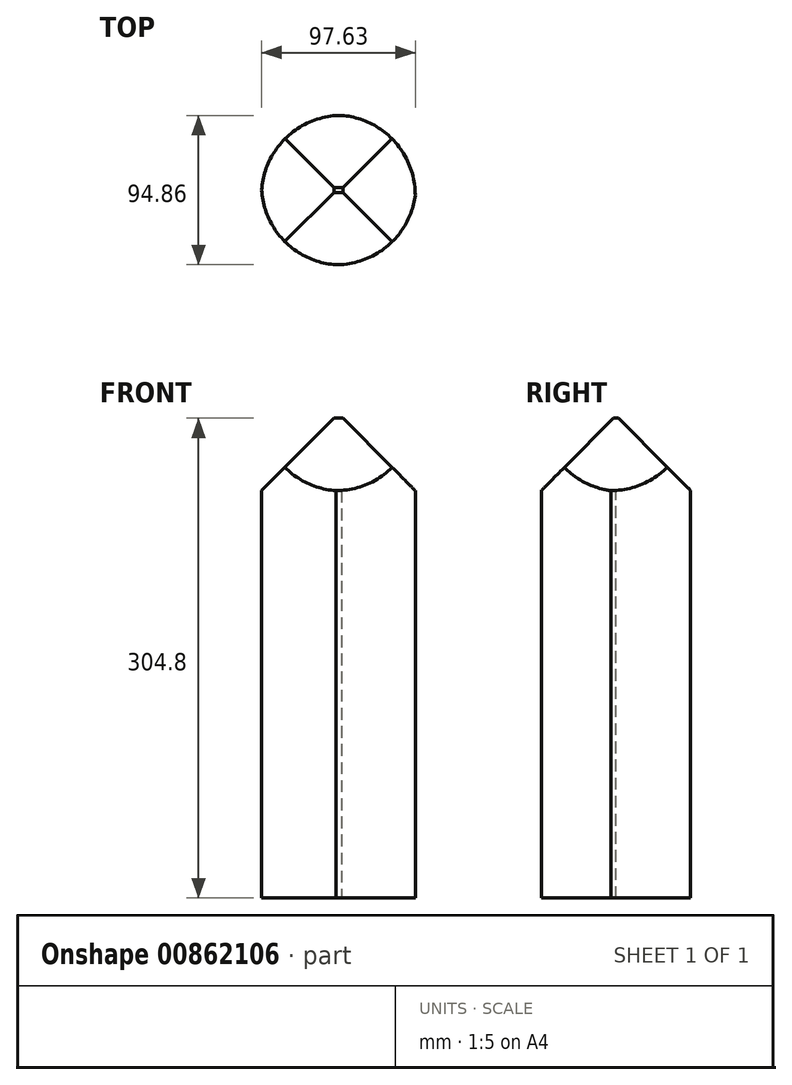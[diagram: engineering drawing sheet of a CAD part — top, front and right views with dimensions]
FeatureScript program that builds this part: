
annotation { "Feature Type Name" : "Feature", "Feature Type Description" : "" }
export const myFeature = defineFeature(function(context is Context, id is Id, definition is map)
    precondition{}
    {
        {
            var Q0;
            Q0=qCreatedBy(makeId("Top.planeOp"),FACE);
            var sketch = newSketch(context, id + "F0", { "sketchPlane" : qUnion([Q0])});
            skLineSegment(sketch, "E0.bottom", {"start": v(-74.27, 76.89) * mm, "end": v(-45.44, 76.89) * mm});
            skLineSegment(sketch, "E0.top", {"start": v(-74.27, 39.29) * mm, "end": v(-45.44, 39.29) * mm});
            skLineSegment(sketch, "E0.left", {"start": v(-74.27, 76.89) * mm, "end": v(-74.27, 39.29) * mm});
            skLineSegment(sketch, "E0.right", {"start": v(-45.44, 76.89) * mm, "end": v(-45.44, 39.29) * mm});
            skLineSegment(sketch, "E1.bottom", {"start": v(-45.44, 39.29) * mm, "end": v(52.3, 39.29) * mm});
            skLineSegment(sketch, "E1.top", {"start": v(-45.44, -55.57) * mm, "end": v(52.3, -55.57) * mm});
            skLineSegment(sketch, "E1.left", {"start": v(-45.44, 39.29) * mm, "end": v(-45.44, -55.57) * mm});
            skLineSegment(sketch, "E1.right", {"start": v(52.3, 39.29) * mm, "end": v(52.3, -55.57) * mm});
            skSolve(sketch);
        }
        {
            var Q0;
            Q0=makeQuery(id+"F0.imprint","IMPRINT",FACE,{"disambiguationData":[TD([[makeQuery(id+"F0.imprint","IMPRINT",EDGE,{"derivedFrom":sQuery(id+"F0.wireOp",EDGE,"E1.bottom")}),-1.0]])]});
            var Q1;
            Q1=makeQuery(id+"F0.imprint","IMPRINT",FACE,{"disambiguationData":[TD([[makeQuery(id+"F0.imprint","IMPRINT",EDGE,{"derivedFrom":sQuery(id+"F0.wireOp",EDGE,"E0.bottom")}),-1.0]])]});
            extrude(context, id + "F1", {"entities" : qUnion([Q0, Q1]), "depth" : 304.8 * mm, "offsetDistance" : 25.4 * mm});
        }
        {
            var Q0;
            Q0=makeQuery(id+"F1.opExtrude","SWEPT_FACE",FACE,{"disambiguationData":[OSD([sQuery(id+"F0.wireOp",EDGE,"E1.right")])]});
            var sketch = newSketch(context, id + "F2", { "sketchPlane" : qUnion([Q0])});
            skLineSegment(sketch, "E2.bottom", {"start": v(-15.23, 174.67) * mm, "end": v(-55.57, 174.67) * mm});
            skLineSegment(sketch, "E2.top", {"start": v(-15.23, 71.74) * mm, "end": v(-55.57, 71.74) * mm});
            skLineSegment(sketch, "E2.left", {"start": v(-15.23, 174.67) * mm, "end": v(-15.23, 71.74) * mm});
            skLineSegment(sketch, "E2.right", {"start": v(-55.57, 174.67) * mm, "end": v(-55.57, 71.74) * mm});
            skSolve(sketch);
        }
        {
            var Q0;
            Q0=makeQuery(id+"F2.imprint","IMPRINT",FACE,{"disambiguationData":[TD([[makeQuery(id+"F2.imprint","IMPRINT",EDGE,{"derivedFrom":sQuery(id+"F2.wireOp",EDGE,"E2.bottom")}),1.0]])]});
            extrude(context, id + "F3", {"entities" : qUnion([Q0]), "operationType" : NewBodyOperationType.ADD, "depth" : -76.2 * mm, "offsetDistance" : 25.4 * mm});
        }
        {
            var Q0;
            Q0=makeQuery(id+"F1.opExtrude","SWEPT_FACE",FACE,{"disambiguationData":[OSD([sQuery(id+"F0.wireOp",EDGE,"E1.top")])]});
            var sketch = newSketch(context, id + "F4", { "sketchPlane" : qUnion([Q0])});
            skCircle(sketch, "E3", {"center": v(0, 202.13) * mm, "radius": 27.07 * mm});
            skSolve(sketch);
        }
        {
            var Q0;
            Q0=sQuery(id+"F4.wireOp",EDGE,"E3");
            extrude(context, id + "F5", {"bodyType" : ToolBodyType.SURFACE, "surfaceEntities" : qUnion([Q0]), "depth" : 304.8 * mm, "offsetDistance" : 25.4 * mm});
        }
        {
            var Q0;
            Q0=makeQuery(id+"F5.opExtrude","SWEPT_BODY",BODY,{"disambiguationData":[OSD([sQuery(id+"F4.wireOp",EDGE,"E3")])]});
            deleteBodies(context, id + "F6", {"entities" : qUnion([Q0])});
        }
        {
            var Q0;
            Q0=makeQuery(id+"F1.opExtrude","SWEPT_BODY",BODY,{"disambiguationData":[OSD([sQuery(id+"F0.wireOp",EDGE,"E0.bottom"),sQuery(id+"F0.wireOp",EDGE,"E0.top"),sQuery(id+"F0.wireOp",EDGE,"E0.left"),sQuery(id+"F0.wireOp",EDGE,"E0.right")])]});
            deleteBodies(context, id + "F7", {"entities" : qUnion([Q0])});
        }
        {
            var Q0;
            Q0=makeQuery(id+"F1.opExtrude","CAP_FACE",FACE,{"disambiguationData":[OSD([sQuery(id+"F0.wireOp",EDGE,"E1.bottom"),sQuery(id+"F0.wireOp",EDGE,"E1.top"),sQuery(id+"F0.wireOp",EDGE,"E1.left"),sQuery(id+"F0.wireOp",EDGE,"E1.right")])],"isStart":false});
            chamfer(context, id + "F8", {"entities" : qUnion([Q0]), "width" : 45.97 * mm, "tangentPropagation" : true});
        }
        {
            var Q0;
            Q0=makeQuery(id+"F1.opExtrude","SWEPT_EDGE",EDGE,{"disambiguationData":[OSD([sQuery(id+"F0.wireOp",EDGE,"E0.top"),sQuery(id+"F0.wireOp",EDGE,"E0.right"),sQuery(id+"F0.wireOp",EDGE,"E1.bottom"),sQuery(id+"F0.wireOp",EDGE,"E1.left")]),OD(1.0)]});
            fillet(context, id + "F9", {"entities" : qUnion([Q0]), "radius" : 50.8 * mm, "tangentPropagation" : true, "allowEdgeOverflow" : false});
        }
        {
            var Q0;
            Q0=makeQuery(id+"F1.opExtrude","SWEPT_EDGE",EDGE,{"disambiguationData":[OSD([sQuery(id+"F0.wireOp",EDGE,"E1.bottom"),sQuery(id+"F0.wireOp",EDGE,"E1.right")])]});
            fillet(context, id + "F10", {"entities" : qUnion([Q0]), "radius" : 50.8 * mm, "tangentPropagation" : true, "allowEdgeOverflow" : false});
        }
        {
            var Q0;
            Q0=makeQuery(id+"F1.opExtrude","SWEPT_EDGE",EDGE,{"disambiguationData":[OSD([sQuery(id+"F0.wireOp",EDGE,"E1.top"),sQuery(id+"F0.wireOp",EDGE,"E1.right")])]});
            fillet(context, id + "F11", {"entities" : qUnion([Q0]), "radius" : 50.8 * mm, "tangentPropagation" : true, "allowEdgeOverflow" : false});
        }
        {
            var Q0;
            Q0=makeQuery(id+"F1.opExtrude","SWEPT_EDGE",EDGE,{"disambiguationData":[OSD([sQuery(id+"F0.wireOp",EDGE,"E1.top"),sQuery(id+"F0.wireOp",EDGE,"E1.left")])]});
            fillet(context, id + "F12", {"entities" : qUnion([Q0]), "radius" : 50.8 * mm, "tangentPropagation" : true, "allowEdgeOverflow" : false});
        }
    });
